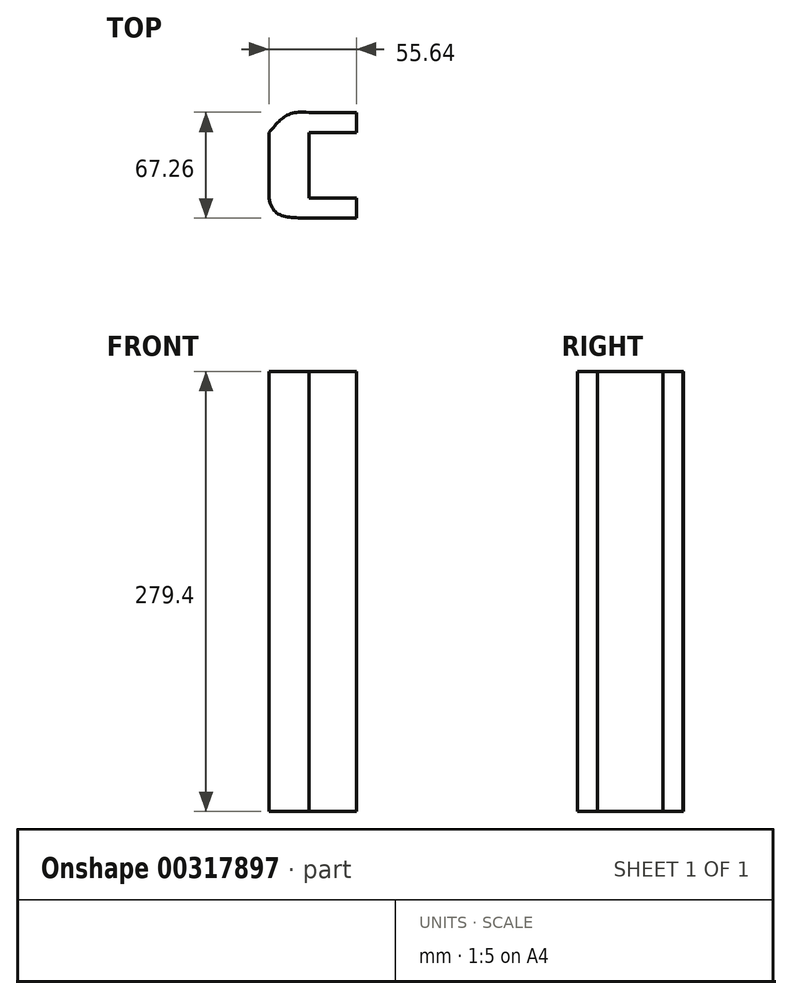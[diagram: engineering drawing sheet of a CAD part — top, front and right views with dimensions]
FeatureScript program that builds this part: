
annotation { "Feature Type Name" : "Feature", "Feature Type Description" : "" }
export const myFeature = defineFeature(function(context is Context, id is Id, definition is map)
    precondition{}
    {
        {
            var Q0;
            Q0=qCreatedBy(makeId("Top.planeOp"),FACE);
            var sketch = newSketch(context, id + "F0", { "sketchPlane" : qUnion([Q0])});
            skLineSegment(sketch, "E0.bottom", {"start": v(-7.82, 19.66) * mm, "end": v(17.58, 19.66) * mm});
            skLineSegment(sketch, "E0.top", {"start": v(-7.82, -21.93) * mm, "end": v(17.58, -21.93) * mm});
            skLineSegment(sketch, "E0.left", {"start": v(-7.82, 19.66) * mm, "end": v(-7.82, -21.93) * mm});
            skLineSegment(sketch, "E0.right", {"start": v(17.58, 19.66) * mm, "end": v(17.58, -21.93) * mm});
            skLineSegment(sketch, "E1.bottom", {"start": v(17.58, 19.66) * mm, "end": v(47.82, 19.66) * mm});
            skLineSegment(sketch, "E1.top", {"start": v(17.58, 32.36) * mm, "end": v(47.82, 32.36) * mm});
            skLineSegment(sketch, "E1.left", {"start": v(17.58, 19.66) * mm, "end": v(17.58, 32.36) * mm});
            skLineSegment(sketch, "E1.right", {"start": v(47.82, 19.66) * mm, "end": v(47.82, 32.36) * mm});
            skLineSegment(sketch, "E2.bottom", {"start": v(17.58, -21.93) * mm, "end": v(47.82, -21.93) * mm});
            skLineSegment(sketch, "E2.top", {"start": v(17.58, -34.63) * mm, "end": v(47.82, -34.63) * mm});
            skLineSegment(sketch, "E2.left", {"start": v(17.58, -16.08) * mm, "end": v(17.58, -34.63) * mm});
            skLineSegment(sketch, "E2.right", {"start": v(47.82, -21.93) * mm, "end": v(47.82, -34.63) * mm});
            skFitSpline(sketch, "E3", {"points": [v(-7.82, -21.93) * mm, v(17.58, -34.63) * mm], "startDerivative": vector(6.38, -40.05) * mm, "endDerivative": vector(38.99, -1.06) * mm});
            skFitSpline(sketch, "E4", {"points": [v(-7.82, 19.66) * mm, v(17.58, 32.36) * mm], "startDerivative": vector(23.46, 26.75) * mm, "endDerivative": vector(43.34, -4.7) * mm});
            skSolve(sketch);
        }
        {
            var Q0;
            Q0 = qSketchRegion(id + "F0", true);
            extrude(context, id + "F1", {"entities" : qUnion([Q0]), "depth" : 254 * mm});
        }
        {
            var Q0;
            Q0=makeQuery(id+"F1.opExtrude","CAP_FACE",FACE,{"disambiguationData":[OSD([sQuery(id+"F0.wireOp",EDGE,"E0.left"),sQuery(id+"F0.wireOp",EDGE,"E0.right"),sQuery(id+"F0.wireOp",EDGE,"E1.bottom"),sQuery(id+"F0.wireOp",EDGE,"E1.top"),sQuery(id+"F0.wireOp",EDGE,"E1.right"),sQuery(id+"F0.wireOp",EDGE,"E2.bottom"),sQuery(id+"F0.wireOp",EDGE,"E2.top"),sQuery(id+"F0.wireOp",EDGE,"E2.left"),sQuery(id+"F0.wireOp",EDGE,"E2.right"),sQuery(id+"F0.wireOp",EDGE,"E3"),sQuery(id+"F0.wireOp",EDGE,"E4")])],"isStart":false});
            extrude(context, id + "F2", {"entities" : qUnion([Q0]), "operationType" : NewBodyOperationType.ADD, "depth" : 25.4 * mm});
        }
    });
